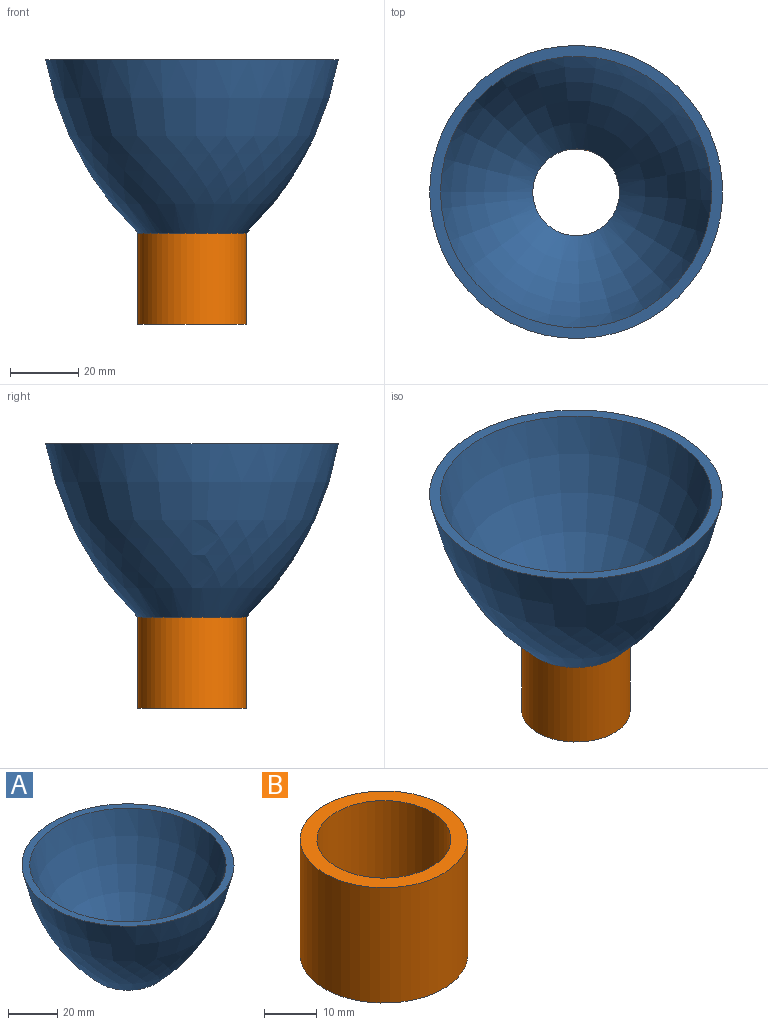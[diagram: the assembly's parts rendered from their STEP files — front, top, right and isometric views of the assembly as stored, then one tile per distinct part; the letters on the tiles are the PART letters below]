
ASSEMBLY  parts=2 mates=1
PART A: 4 faces, bbox 85.8x85.8x50.8 mm
  f0: plane 85.8x85.8mm, normal (0,0,1), area 824.1mm2, adj f1,f3
  f1: revolved ~85.8x85.8mm, area 11772.7mm2, adj f0,f2
  f2: plane 31.75x31.75mm, normal (0,0,-1), area 285mm2, adj f1,f3
  f3: revolved ~79.45x79.45mm, area 10484.1mm2, adj f0,f2
PART B: 4 faces, bbox 31.8x31.8x26.7 mm
  f0: cylinder r=15.88mm len=31.75mm, axis (0,0,-1), area 2667.7mm2, adj f1,f3
  f1: plane 31.75x31.75mm, normal (0,0,1), area 285mm2, adj f0,f2
  f2: cylinder r=12.7mm len=26.75mm, axis (0,0,-1), area 2134.2mm2, adj f1,f3
  f3: plane 31.75x31.75mm, normal (0,0,-1), area 285mm2, adj f0,f2
PLACE A t=(-51.05,-40.09,-3.22)mm
PLACE B t=(-51.05,-40.09,-29.97)mm
MATE fastened B.f0 <-> A.f2  axis (0,0,-1) through (-51.05,-40.09,-3.22)mm
